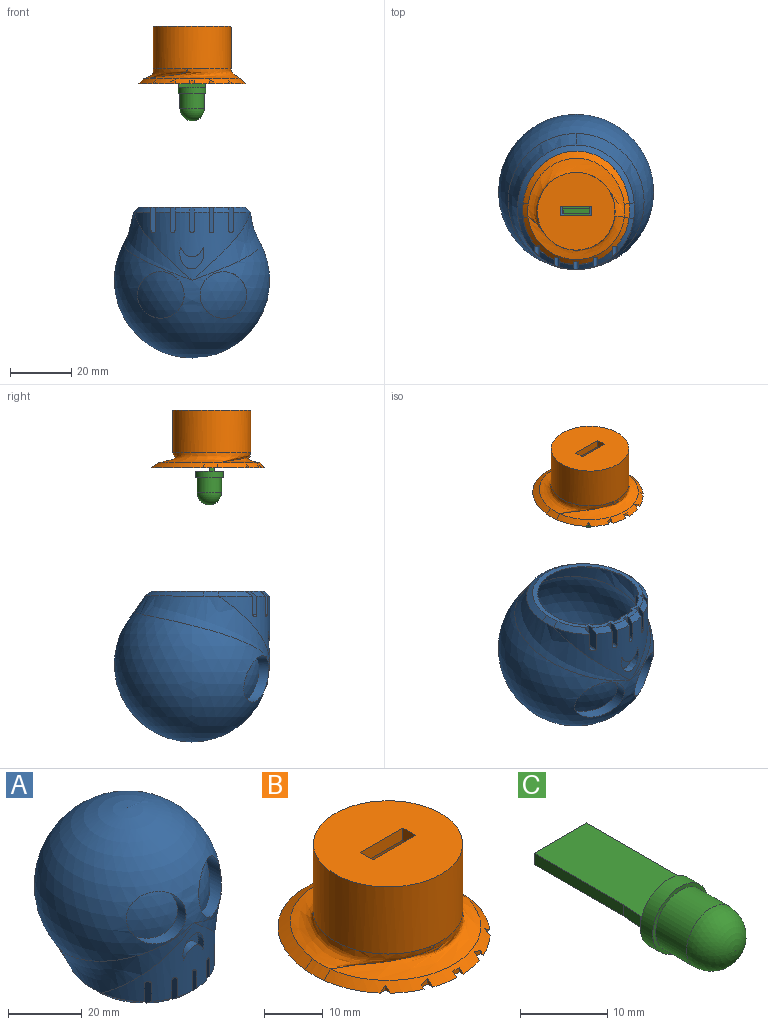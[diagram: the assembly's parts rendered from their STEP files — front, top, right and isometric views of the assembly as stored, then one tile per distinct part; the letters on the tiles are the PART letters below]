
ASSEMBLY  parts=3 mates=2
PART A: 81 faces, bbox 52.8x52.8x61.2 mm
  f0: cone r=17.46mm half-angle=45deg, axis (0,0,1), area 25.6mm2, adj f14,f15,f25,f37,f40
  f1: cone r=17.46mm half-angle=45deg, axis (0,0,1), area 13mm2, adj f12,f23,f25,f40
  f2: cone r=17.46mm half-angle=45deg, axis (0,0,1), area 11.2mm2, adj f21,f25,f30,f40
  f3: cone r=17.46mm half-angle=45deg, axis (0,0,1), area 11.2mm2, adj f19,f25,f31,f40
  f4: cone r=17.46mm half-angle=45deg, axis (0,0,1), area 13mm2, adj f11,f17,f25,f40
  f5: bspline ~44.85x33.75mm, area 473.2mm2, adj f25,f35,f36,f38,f39
  f6: sphere r=22.23mm, area 119.9mm2, adj f34
  f7: sphere r=22.23mm, area 119.7mm2, adj f33
  f8: plane 8.29x1.53mm, normal (0,-1,0), area 12.4mm2, adj f9,f10,f11,f16,f40
  f9: plane 7.4x2.14mm, normal (1,0,0), area 13.6mm2, adj f8,f10,f16,f25
  f10: cylinder r=0.76mm len=3.42mm, axis (0,1,0), area 6.5mm2, adj f8,f9,f11,f25
  f11: plane 7.64x3.51mm, normal (-1,0,0), area 24mm2, adj f4,f8,f10,f25,f40
  f12: plane 7.64x3.51mm, normal (1,0,0), area 24mm2, adj f1,f13,f15,f25,f40
  f13: cylinder r=0.76mm len=3.42mm, axis (0,1,0), area 6.5mm2, adj f12,f14,f15,f25
  f14: plane 7.4x2.14mm, normal (-1,0,0), area 13.6mm2, adj f0,f13,f15,f25
  f15: plane 8.29x1.53mm, normal (0,-1,0), area 12.4mm2, adj f0,f12,f13,f14,f40
  f16: cone r=17.46mm half-angle=45deg, axis (0,0,1), area 25.4mm2, adj f8,f9,f25,f36,f40
  f17: plane 7.6x2.49mm, normal (1,0,0), area 16.9mm2, adj f4,f18,f20,f25,f40
  f18: cylinder r=0.76mm len=2.97mm, axis (0,1,0), area 6.5mm2, adj f17,f19,f20,f25
  f19: plane 7.6x3.03mm, normal (-1,0,0), area 21mm2, adj f3,f18,f20,f25,f40
  f20: plane 8.29x1.52mm, normal (0,-1,0), area 12.4mm2, adj f17,f18,f19,f40
  f21: plane 7.6x3.03mm, normal (1,0,0), area 21mm2, adj f2,f22,f24,f25,f40
  f22: cylinder r=0.76mm len=2.97mm, axis (0,1,0), area 6.5mm2, adj f21,f23,f24,f25
  f23: plane 7.6x2.49mm, normal (-1,0,0), area 16.9mm2, adj f1,f22,f24,f25,f40
  f24: plane 8.29x1.52mm, normal (0,-1,0), area 12.4mm2, adj f21,f22,f23,f40
  f25: cylinder r=19.05mm len=37.8mm, axis (0,0,1), area 495.5mm2, adj f0,f1,f2,f3,f4,f5,f9,f10
  f26: extruded ~7.94x7.13mm, area 43.4mm2, adj f25,f27,f28
  f27: extruded ~7.33x3.16mm, area 24.4mm2, adj f25,f26,f28
  f28: plane 8.03x7.22mm, normal (0,-1,0), area 30.7mm2, adj f26,f27
  f29: cylinder r=0.76mm len=2.54mm, axis (0,1,0), area 6.1mm2, adj f25,f30,f31,f32
  f30: plane 7.53x2.53mm, normal (-1,0,0), area 17.7mm2, adj f2,f25,f29,f32,f40
  f31: plane 7.53x2.53mm, normal (1,0,0), area 17.7mm2, adj f3,f25,f29,f32,f40
  f32: plane 8.29x1.52mm, normal (0,-1,0), area 12.4mm2, adj f29,f30,f31,f40
  f33: cylinder r=7.62mm len=15.26mm, axis (0,1,0), area 193.6mm2, adj f7,f39
  f34: cylinder r=7.62mm len=15.26mm, axis (0,1,0), area 160.6mm2, adj f6,f39
  f35: bspline ~38.05x19.1mm, area 142.9mm2, adj f5,f36,f37,f38,f40
  f36: bspline ~5.18x3.46mm, area 11.3mm2, adj f5,f16,f35,f40
  f37: bspline ~5.13x1.79mm, area 11.3mm2, adj f0,f35,f38,f40
  f38: bspline ~44.45x33.6mm, area 553.7mm2, adj f5,f25,f35,f37,f39
  f39: sphere r=25.4mm, area 5560.3mm2, adj f5,f33,f34,f38
  f40: plane 37.45x35.37mm, normal (0,0,-1), area 166.8mm2, adj f0,f1,f2,f3,f4,f8,f11,f12
  f41: sphere r=21.23mm, area 312.5mm2, adj f44
  f42: sphere r=21.23mm, area 313mm2, adj f45
  f43: plane 12.62x11.18mm, normal (0,1,0), area 66.3mm2, adj f47,f48
  f44: cylinder r=8.62mm len=17.26mm, axis (0,1,0), area 240.1mm2, adj f41,f46,f49
  f45: cylinder r=8.62mm len=17.26mm, axis (0,1,0), area 242.6mm2, adj f42,f46,f50
  f46: sphere r=24.4mm, area 4821.9mm2, adj f44,f45,f49,f50
  f47: extruded ~11.39x9.92mm, area 67.3mm2, adj f43,f48,f58
  f48: extruded ~7.01x5.42mm, area 32.8mm2, adj f43,f47,f58
  f49: offset ~46.45x35.6mm, area 498mm2, adj f44,f46,f50,f58,f61,f78,f79
  f50: offset ~46.45x35.6mm, area 497.8mm2, adj f45,f46,f49,f58,f61,f77,f80
  f51: plane 5.73x0.37mm, normal (1,0,0), area 2.1mm2, adj f57,f58,f76,f77
  f52: cylinder r=1.76mm len=3.53mm, axis (0,1,0), area 14.1mm2, adj f53,f58,f74,f75
  f53: plane 7.22x1.93mm, normal (-1,0,0), area 12mm2, adj f52,f58,f64,f75
  f54: cylinder r=1.76mm len=3.53mm, axis (0,1,0), area 13.8mm2, adj f58,f66,f72,f73
  f55: cylinder r=1.76mm len=3.53mm, axis (0,1,0), area 14.1mm2, adj f56,f58,f68,f71
  f56: plane 7.22x1.93mm, normal (1,0,0), area 12mm2, adj f55,f58,f70,f71
  f57: cylinder r=1.76mm len=3.93mm, axis (0,1,0), area 12.6mm2, adj f51,f58,f69,f76
  f58: cylinder r=18.05mm len=35.65mm, axis (0,0,1), area 336.3mm2, adj f47,f48,f49,f50,f51,f52,f53,f54
  f59: cylinder r=1.76mm len=3.93mm, axis (0,1,0), area 12.6mm2, adj f58,f60,f62,f63
  f60: plane 5.73x0.37mm, normal (-1,0,0), area 2.1mm2, adj f58,f59,f62,f78
  f61: offset ~40.05x21.56mm, area 178mm2, adj f40,f49,f50,f79,f80
  f62: plane 9.38x3.61mm, normal (0,1,0), area 29.4mm2, adj f40,f59,f60,f63,f78
  f63: plane 7.65x4.05mm, normal (1,0,0), area 27mm2, adj f40,f58,f59,f62,f64
  f64: cone r=16.76mm half-angle=45deg, axis (0,0,1), area 10.1mm2, adj f40,f53,f58,f63,f75
  f65: cone r=16.76mm half-angle=45deg, axis (0,0,1), area 8.2mm2, adj f40,f58,f66,f74
  f66: plane 7.54x2.47mm, normal (-1,0,0), area 16.4mm2, adj f40,f54,f58,f65,f73
  f67: cone r=16.76mm half-angle=45deg, axis (0,0,1), area 8.2mm2, adj f40,f58,f68,f72
  f68: plane 7.56x3.25mm, normal (-1,0,0), area 22.1mm2, adj f40,f55,f58,f67,f71
  f69: plane 7.65x4.05mm, normal (-1,0,0), area 27mm2, adj f40,f57,f58,f70,f76
  f70: cone r=16.76mm half-angle=45deg, axis (0,0,1), area 10.1mm2, adj f40,f56,f58,f69,f71
  f71: plane 9.3x3.54mm, normal (0,1,0), area 31.3mm2, adj f40,f55,f56,f68,f70
  f72: plane 7.54x2.47mm, normal (1,0,0), area 16.4mm2, adj f40,f54,f58,f67,f73
  f73: plane 9.29x3.52mm, normal (0,1,0), area 31.4mm2, adj f40,f54,f66,f72
  f74: plane 7.56x3.25mm, normal (1,0,0), area 22.1mm2, adj f40,f52,f58,f65,f75
  f75: plane 9.3x3.54mm, normal (0,1,0), area 31.3mm2, adj f40,f52,f53,f64,f74
  f76: plane 9.38x3.61mm, normal (0,1,0), area 29.4mm2, adj f40,f51,f57,f69,f77
  f77: cone r=16.76mm half-angle=45deg, axis (0,0,1), area 26.2mm2, adj f40,f50,f51,f58,f76,f80
  f78: cone r=16.76mm half-angle=45deg, axis (0,0,1), area 26.1mm2, adj f40,f49,f58,f60,f62,f79
  f79: offset ~7.18x5.71mm, area 13.5mm2, adj f40,f49,f61,f78
  f80: offset ~7.18x5.71mm, area 13.5mm2, adj f40,f50,f61,f77
PART B: 50 faces, bbox 40.2x41.2x22.4 mm
  f0: plane 3x2.54mm, normal (1,0,0), area 7.6mm2, adj f1,f3,f27,f28
  f1: plane 10.16x2.54mm, normal (0,1,0), area 25.8mm2, adj f0,f2,f3,f28
  f2: plane 3x2.54mm, normal (-1,0,0), area 7.6mm2, adj f1,f3,f27,f28
  f3: plane 20.32x20.32mm, normal (0,0,-1), area 293.8mm2, adj f0,f1,f2,f4,f27
  f4: cylinder r=10.16mm len=20.32mm, axis (0,0,1), area 1021.5mm2, adj f3,f6
  f5: extruded ~25.06x6.78mm, area 0mm2, adj f6,f7
  f6: plane 33.01x31.56mm, normal (0,0,-1), area 487.8mm2, adj f4,f5,f7,f8,f9,f10,f11,f12
  f7: offset ~40.05x21.61mm, area 26mm2, adj f5,f6,f25,f26,f49
  f8: plane 1.24x0.3mm, normal (0,1,0), area 0.3mm2, adj f6,f9,f24,f49
  f9: plane 1.29x0.3mm, normal (-1,0,0), area 0.3mm2, adj f6,f8,f10,f49
  f10: cone r=16.76mm half-angle=45deg, axis (0,0,-1), area 2mm2, adj f6,f9,f21,f49
  f11: cone r=16.76mm half-angle=45deg, axis (0,0,-1), area 1.2mm2, adj f6,f12,f20,f49
  f12: plane 0.42x0.3mm, normal (1,0,0), area 0.1mm2, adj f6,f11,f19,f49
  f13: cone r=16.76mm half-angle=45deg, axis (0,0,-1), area 1.2mm2, adj f6,f14,f18,f49
  f14: plane 1.12x0.3mm, normal (1,0,0), area 0.3mm2, adj f6,f13,f17,f49
  f15: plane 1.29x0.3mm, normal (1,0,0), area 0.3mm2, adj f6,f16,f22,f49
  f16: cone r=16.76mm half-angle=45deg, axis (0,0,-1), area 2mm2, adj f6,f15,f17,f49
  f17: plane 2.79x0.31mm, normal (0,1,0), area 0.7mm2, adj f6,f14,f16,f49
  f18: plane 0.42x0.3mm, normal (-1,0,0), area 0.1mm2, adj f6,f13,f19,f49
  f19: plane 3.52x0.3mm, normal (0,1,0), area 1.1mm2, adj f6,f12,f18,f49
  f20: plane 1.12x0.3mm, normal (-1,0,0), area 0.3mm2, adj f6,f11,f21,f49
  f21: plane 2.79x0.31mm, normal (0,1,0), area 0.7mm2, adj f6,f10,f20,f49
  f22: plane 1.24x0.3mm, normal (0,1,0), area 0.3mm2, adj f6,f15,f23,f49
  f23: cone r=16.76mm half-angle=45deg, axis (0,0,-1), area 4mm2, adj f6,f22,f26,f49
  f24: cone r=16.76mm half-angle=45deg, axis (0,0,-1), area 4mm2, adj f6,f8,f25,f49
  f25: offset ~6.49x2.46mm, area 1.8mm2, adj f6,f7,f24,f49
  f26: offset ~7.18x5.71mm, area 1.8mm2, adj f6,f7,f23,f49
  f27: plane 10.16x2.54mm, normal (0,-1,0), area 25.8mm2, adj f0,f2,f3,f28
  f28: plane 25.4x25.4mm, normal (0,0,1), area 476.2mm2, adj f0,f1,f2,f27,f29
  f29: cylinder r=12.7mm len=25.4mm, axis (0,0,1), area 1114.8mm2, adj f28,f30,f31
  f30: bspline ~31.5x14.64mm, area 189.8mm2, adj f29,f31,f44
  f31: bspline ~31.75x29.93mm, area 358.2mm2, adj f29,f30,f41,f42,f43
  f32: plane 1.57x1.26mm, normal (0,-1,0), area 1.4mm2, adj f33,f34,f44,f49
  f33: plane 1.33x1.25mm, normal (1,0,0), area 0.8mm2, adj f32,f44,f49
  f34: plane 0.7x0.64mm, normal (-1,0,0), area 0.2mm2, adj f32,f44,f49
  f35: plane 1.57x0.98mm, normal (0,-1,0), area 1.4mm2, adj f36,f37,f44,f49
  f36: plane 0.92x0.92mm, normal (-1,0,0), area 0.4mm2, adj f35,f44,f49
  f37: plane 0.92x0.92mm, normal (1,0,0), area 0.4mm2, adj f35,f44,f49
  f38: plane 1.57x1.26mm, normal (0,-1,0), area 1.4mm2, adj f39,f40,f44,f49
  f39: plane 0.7x0.64mm, normal (1,0,0), area 0.2mm2, adj f38,f44,f49
  f40: plane 1.33x1.25mm, normal (-1,0,0), area 0.8mm2, adj f38,f44,f49
  f41: bspline ~5.13x3.46mm, area 10mm2, adj f31,f43,f44,f49
  f42: bspline ~4.69x1.75mm, area 10mm2, adj f31,f43,f44,f49
  f43: bspline ~34.71x17.17mm, area 125.6mm2, adj f31,f41,f42,f49
  f44: cone r=17.46mm half-angle=45deg, axis (0,0,-1), area 98.4mm2, adj f30,f32,f33,f34,f35,f36,f37,f38
  f45: plane 1.28x0.96mm, normal (0,-1,0), area 0.6mm2, adj f44,f46,f49
  f46: plane 1.33x0.96mm, normal (-1,0,0), area 0.6mm2, adj f44,f45,f49
  f47: plane 1.33x0.96mm, normal (1,0,0), area 0.6mm2, adj f44,f48,f49
  f48: plane 1.28x0.96mm, normal (0,-1,0), area 0.6mm2, adj f44,f47,f49
  f49: plane 37.45x35.37mm, normal (0,0,-1), area 166.8mm2, adj f7,f8,f9,f10,f11,f12,f13,f14
PART C: 15 faces, bbox 9x28.5x9 mm
  f0: plane 1.57x0.28mm, normal (0,-1,0), area 0.1mm2, adj f2,f7,f12
  f1: plane 14.47x1.57mm, normal (-1,0,0), area 22.7mm2, adj f2,f6,f7,f8
  f2: plane 3x1.57mm, normal (-1,0.08,0), area 4.7mm2, adj f0,f1,f7,f8
  f3: plane 1.57x0.28mm, normal (0,-1,0), area 0.1mm2, adj f4,f7,f12
  f4: plane 3x1.57mm, normal (1,0.08,0), area 4.7mm2, adj f3,f5,f7,f8
  f5: plane 14.47x1.57mm, normal (1,0,0), area 22.7mm2, adj f4,f6,f7,f8
  f6: plane 8.54x1.57mm, normal (0,1,0), area 13.4mm2, adj f1,f5,f7,f8
  f7: plane 17.47x9mm, normal (0,0,1), area 149.9mm2, adj f0,f1,f2,f3,f4,f5,f6,f9
  f8: plane 17.47x9mm, normal (0,0,-1), area 149.9mm2, adj f1,f2,f4,f5,f6,f13
  f9: plane 8.43x2.93mm, normal (0,1,0), area 18mm2, adj f7,f12
  f10: cylinder r=4mm len=8mm, axis (0,1,0), area 125.7mm2, adj f11,f14
  f11: plane 9x9mm, normal (0,-1,0), area 13.4mm2, adj f10,f12
  f12: cylinder r=4.5mm len=9mm, axis (0,1,0), area 56.5mm2, adj f0,f3,f9,f11,f13
  f13: plane 9x4.5mm, normal (0,1,0), area 31.8mm2, adj f8,f12
  f14: sphere r=4mm, area 100.5mm2, adj f10
PLACE A rot(axis=(0,1,0),180deg) t=(-66.4,-7.58,15.41)mm fixed
PLACE B t=(-15.81,-7.59,55.76)mm
PLACE C rot(axis=(1,0,0),90deg) t=(-114.07,-13.27,10.82)mm
MATE slider A.f40 <-> B.f49  axis (0,0,1) through (-66.38,-30.44,15.36)mm
MATE slider B.f4 <-> C.f6  axis (0,0,-1) through (-66.36,-14.05,72.1)mm
